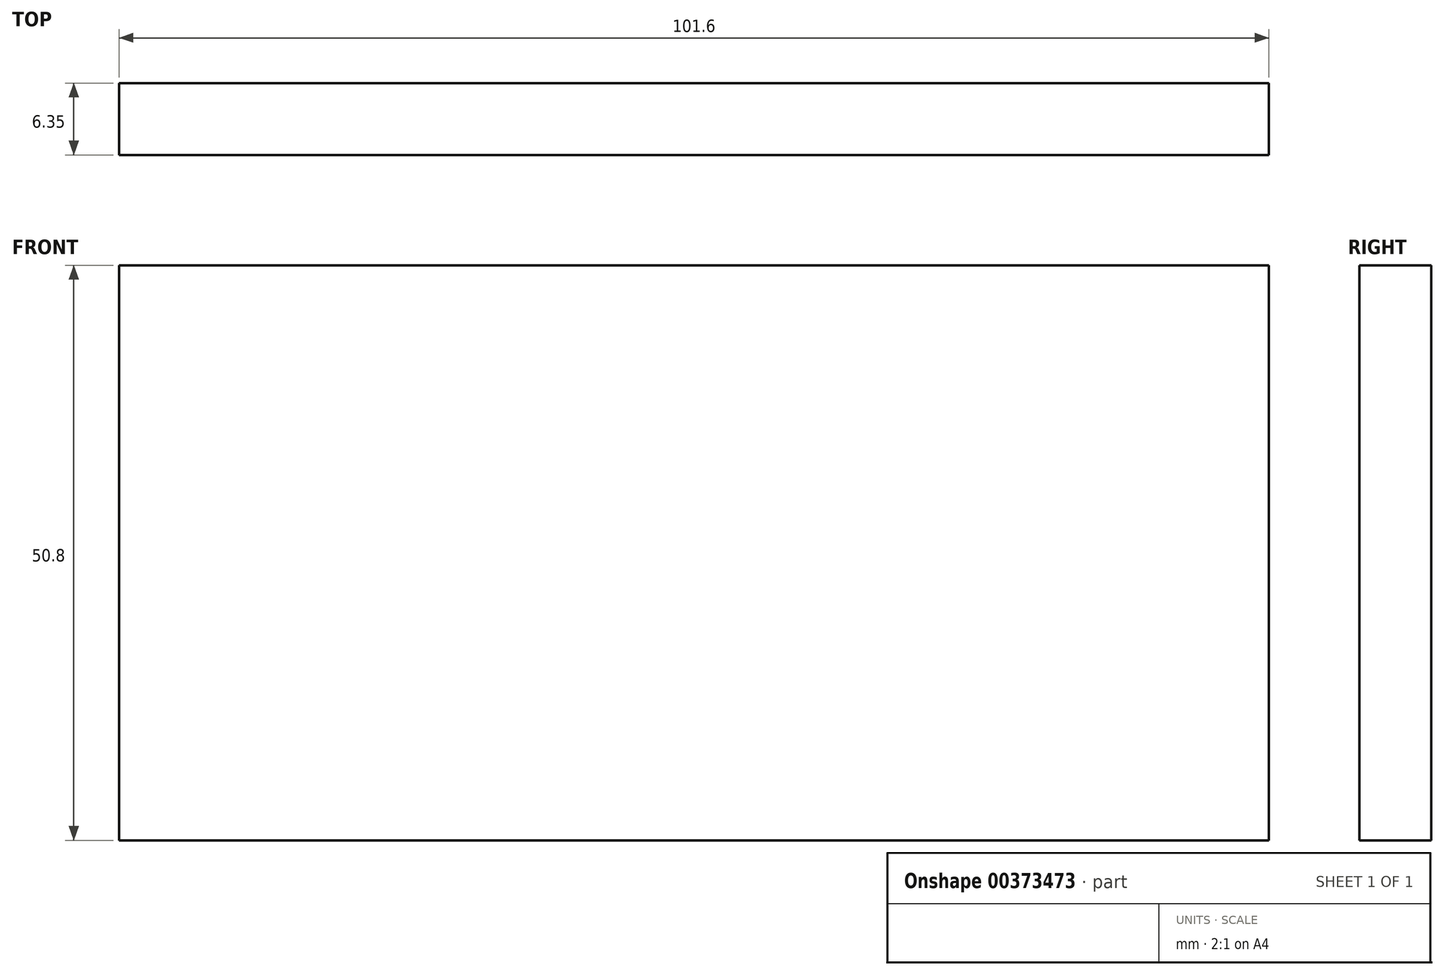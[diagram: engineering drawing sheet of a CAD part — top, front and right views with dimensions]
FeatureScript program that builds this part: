
annotation { "Feature Type Name" : "Feature", "Feature Type Description" : "" }
export const myFeature = defineFeature(function(context is Context, id is Id, definition is map)
    precondition{}
    {
        {
            var Q0;
            Q0=qCreatedBy(makeId("Front.planeOp"),FACE);
            var sketch = newSketch(context, id + "F0", { "sketchPlane" : qUnion([Q0])});
            skLineSegment(sketch, "E0", {"start": v(-51.15, 17.07) * mm, "end": v(-51.15, -33.73) * mm});
            skLineSegment(sketch, "E1", {"start": v(-51.15, -33.73) * mm, "end": v(50.45, -33.73) * mm});
            skLineSegment(sketch, "E2", {"start": v(50.45, -33.73) * mm, "end": v(50.45, 17.07) * mm});
            skLineSegment(sketch, "E3", {"start": v(50.45, 17.07) * mm, "end": v(-51.15, 17.07) * mm});
            skSolve(sketch);
        }
        {
            var Q0;
            Q0 = qSketchRegion(id + "F0", true);
            extrude(context, id + "F1", {"entities" : qUnion([Q0]), "depth" : 6.35 * mm});
        }
    });
